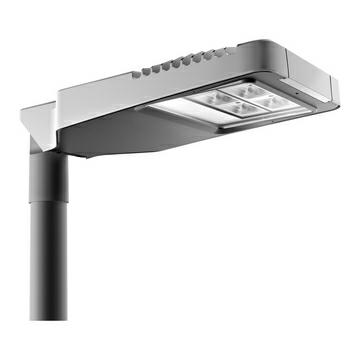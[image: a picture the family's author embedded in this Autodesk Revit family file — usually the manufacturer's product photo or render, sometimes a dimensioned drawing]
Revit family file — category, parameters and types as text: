
# Revit family: Lighting-StreetLighting-GEWISS-ROAD[5]MINI-LED_OPTIC_WIDE-W_NEMA-ZAGA
name_source: partatom
category: Apparecchi per illuminazione
units: mm (PartAtom-declared; Revit-internal decimal feet)

## family parameters
Basato su piano di lavoro = No
Condiviso = No
Punto di calcolo locali = No
Quota connettore circolare = Usa diametro
Sempre verticale = Sì
Sorgente d'illuminazione = No
Taglio con vuoti quando caricato = No
Tipo di parte = Normale

## types (4) — shared parameters
Applicazione = External
Body = Die-cast aluminium -
Carico apparente = 28 VA
Catalogue = LIGHTING
Catalogue Range = ROAD [5]
Classification: = -
Color Rendering Index = CRI-70
Colore = Graphite grey
Colour : = Powder coating
Colour temperature = 4000K
Colour temperature: = 4000 K (CRI>70)
Commenti sul wattaggio = 28W
Context = Street and parking lighting
DIN 18032-3 certification = -
Device with reduced surface temperature = -
Driver = Included
Driver Box = Built-in
Electrocod = 244C
Eletrical and lighting features = -
External screw = Stainless steel
Fixing = Pole Head - Outreach
Gasket = Anti-aging silicone
General information = -
Glow Wire Test : = -
IDF = c974a623-9cd0-4fd8-bd45-dddc2be459b5
IDT = 6ace804b625941958a80978d94961bce
IP degree = IP66
Immagine tipo = GWR5276M.jpg
Installationa and maintenance = -
Insulation class = II
LED Life time (L80B10) = 100000H
LED Maintenance = Not available
LED current. = 0,5A
Lamp- = LED
Lifetime = L90B10 (Tq+25°C) = 100.000 h
Locking Hook = Integrated front handle
Luminaire = LED Road Equipment
Materials = -
Maximum surface exposed to the wind = 0,149999999999999M2
Maximum surface exposed to the wind : = 0.15 m²
Minimum distance from the illuminated object = 1M
Mouting and installation = Pole Head - Outreach
Optic = WIDE
Optic : = Metallized polycarbonate reflector
Optic Maintenance = Not available
Optic and illuminating features = -
Overvoltage protection = DM 10KV / CM 10KV
Overvoltage resistance = 10 KV (Common mode)
Photobiological Risk Class = RG0
Produttore = GEWISS S.p.A.
Rated frequency (Hz) = 50 / 60
SEO = Street lighting
Shield type = 4mm thick flat tempered glass
Shock resistance = IK08
Standard Deviation Colour Matching = SDCM = 5
Standard- = EN 60598-2-3, EN 60598-1 IEC/TR 62778
Standards and approvals = -
Stocking temperature = -
Supply voltage = 220 - 240 V
Technical sheet = https://www.gewiss.com
Tilt adjustable = -20° ÷ +10° side bracket - -10° ÷ +20° pole head
Tilt- = -20° ÷ +10° side bracket - -10° ÷ +20° pole head
Tipo alimentatore = Constant Current Driver Led
Tipologia = Bi power
Type of light source = LED - Not replaceable
URL = https://www.gewiss.com
Unified Glare Rating = G*4 - ULOR = 0
Unique digital code (Datamatrix) = Currently not present
Version file RFA = 20.11
Voltage- = 220 / 240 V - 50 / 60 Hz
Warranty = 5 years
Wiring = Isolating switch

## per-type parameters (varying)
| type | Control System | Efficiency (lm/W) | IPEA | Lumen output (lm) | Modello | Number of modules | Operating temperature : | Operating temperature: | System power | System power : | Weight (kg): |
| GWR5251NW - ROAD5 MINI WIDE 1M 4000K 0,50A CL2 W NEM | Remote management with Nema module | 114 | ROAD = A4 + // LARGE AREAS = A5 + // CYCLOPEDONALS = A4 + // GREEN AREAS = A4 + // HISTORICAL CENTER = A6 + | 4200 | GWR5251NW | 1 (1x3 LED) | -25 +40 °C | -25 +40 °C | 37W | 37 W @ 0.5A | 6,4 |
| GWR5251ZW - ROAD5 MINI WIDE 1M 4000K 0,50A CL2 W ZHA | Remote management with Zhaga module | 114 | ROAD = A4 + // LARGE AREAS = A5 + // CYCLOPEDONALS = A4 + // GREEN AREAS = A4 + // HISTORICAL CENTER = A6 + | 4200 | GWR5251ZW | 1 (1x3 LED) | -25 +40 °C | -25 +40 °C | 37W | 37 W @ 0.5A | 6,4 |
| GWR5252ZW - ROAD5 MINI WIDE 2M 4000K 0,50A CL2 W ZHA | Remote management with Zhaga module | 111 | ROAD = A3 + // LARGE AREAS = A4 + // CYCLOPEDONALS = A ++ // GREEN AREAS = A ++ // HISTORICAL CENTER = A6 + | 8100 | GWR5252ZW | 2 (2x3 LED) | -25 +30 °C | -25 +30 °C | 73W | 73 W @ 0.5A | 6,59999999999999 |
| GWR5252NW - ROAD5 MINI WIDE 2M 4000K 0,50A CL2 W NEM | Remote management with Nema module | 111 | ROAD = A3 + // LARGE AREAS = A4 + // CYCLOPEDONALS = A ++ // GREEN AREAS = A ++ // HISTORICAL CENTER = A6 + | 8100 | GWR5252NW | 2 (2x3 LED) | -25 +30 °C | -25 +30 °C | 73W | 73 W @ 0.5A | 6,59999999999999 |

note: column(s) folded — value = type name in every type: Descrizione

## geometry (parser evidence)
native form markers: Blend x2
no freeform markers — native parametric forms only
